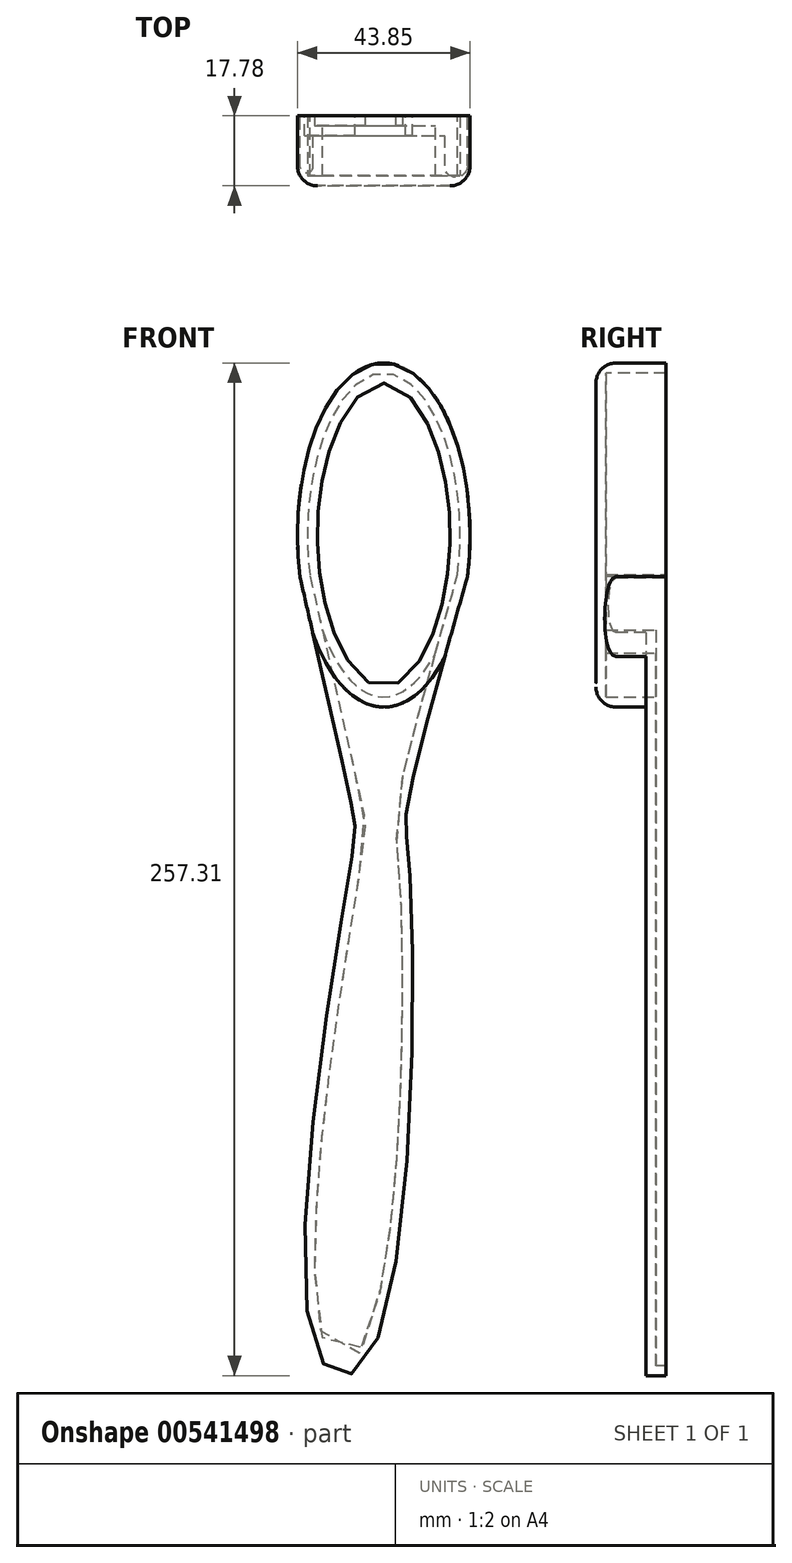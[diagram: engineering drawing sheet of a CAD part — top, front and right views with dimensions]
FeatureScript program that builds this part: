
annotation { "Feature Type Name" : "Feature", "Feature Type Description" : "" }
export const myFeature = defineFeature(function(context is Context, id is Id, definition is map)
    precondition{}
    {
        {
            var Q0;
            Q0=qCreatedBy(makeId("Front.planeOp"),FACE);
            var sketch = newSketch(context, id + "F0", { "sketchPlane" : qUnion([Q0])});
            skEllipse(sketch, "E0", {"center": v(-128.99, 60.04) * mm, "majorRadius": 43.72 * mm, "minorRadius": 21.92 * mm, "majorAxis": v(0, -1)});
            skFitSpline(sketch, "E1", {"points": [v(-150.22, 49.17) * mm, v(-136.9, -9.71) * mm, v(-136.95, -20.7) * mm, v(-146.15, -147.24) * mm, v(-133.54, -149.91) * mm, v(-122.55, -22.87) * mm, v(-123.31, -10.54) * mm, v(-107.71, 49.47) * mm], "startDerivative": vector(106.91, -468.56) * mm, "endDerivative": vector(133.37, 469.07) * mm});
            skSolve(sketch);
        }
        {
            var Q0;
            {var subQ0=sQuery(id+"F0.wireOp",EDGE,"E1");var subQ1=sQuery(id+"F0.wireOp",EDGE,"E0");var subQ2=makeQuery(id+"F0.imprint","INTERSECT",VERTEX,{"disambiguationData":[OD(2.0)],"derivedFrom":[subQ1,subQ0]});Q0=makeQuery(id+"F0.imprint","IMPRINT",FACE,{"disambiguationData":[TD([[makeQuery(id+"F0.imprint","IMPRINT",EDGE,{"disambiguationData":[TD([[subQ2,1.0]])],"derivedFrom":subQ1}),-1.0]])]});}
            extrude(context, id + "F1", {"entities" : qUnion([Q0]), "depth" : 5.08 * mm, "offsetDistance" : 25.4 * mm});
        }
        {
            var Q0;
            {var subQ0=sQuery(id+"F0.wireOp",EDGE,"E1");var subQ1=sQuery(id+"F0.wireOp",EDGE,"E0");var subQ2=makeQuery(id+"F0.imprint","INTERSECT",VERTEX,{"disambiguationData":[OD(0.0)],"derivedFrom":[subQ1,subQ0]});Q0=makeQuery(id+"F0.imprint","IMPRINT",FACE,{"disambiguationData":[TD([[makeQuery(id+"F0.imprint","IMPRINT",EDGE,{"disambiguationData":[TD([[subQ2,1.0]])],"derivedFrom":subQ1}),1.0]])]});}
            extrude(context, id + "F2", {"entities" : qUnion([Q0]), "operationType" : NewBodyOperationType.ADD, "depth" : 17.78 * mm, "offsetDistance" : 25.4 * mm});
        }
        {
            var Q0;
            {var subQ0=sQuery(id+"F0.wireOp",EDGE,"E1");var subQ1=sQuery(id+"F0.wireOp",EDGE,"E0");Q0=makeQuery(id+"F2.boolean.opBoolean","MERGE",FACE,{"derivedFrom":[makeQuery(id+"F1.opExtrude","CAP_FACE",FACE,{"disambiguationData":[OSD([subQ1,subQ0])],"isStart":true}),makeQuery(id+"F2.opExtrude","CAP_FACE",FACE,{"disambiguationData":[OSD([subQ1,subQ0])],"isStart":true})]});}
            shell(context, id + "F3", {"entities" : qUnion([Q0]), "thickness" : 2.54 * mm});
        }
        {
            var Q0;
            {var subQ0=sQuery(id+"F0.wireOp",EDGE,"E1");var subQ1=sQuery(id+"F0.wireOp",EDGE,"E0");Q0=makeQuery(id+"F2.opExtrude","CAP_EDGE",EDGE,{"disambiguationData":[OSD([subQ1]),TDD([makeQuery(id+"F0.imprint","IMPRINT",EDGE,{"disambiguationData":[TD([[makeQuery(id+"F0.imprint","INTERSECT",VERTEX,{"disambiguationData":[OD(0.0)],"derivedFrom":[subQ1,subQ0]}),1.0]])],"derivedFrom":subQ1})])],"isStart":false});}
            fillet(context, id + "F4", {"entities" : qUnion([Q0]), "radius" : 5.08 * mm, "tangentPropagation" : true, "allowEdgeOverflow" : false});
        }
    });
